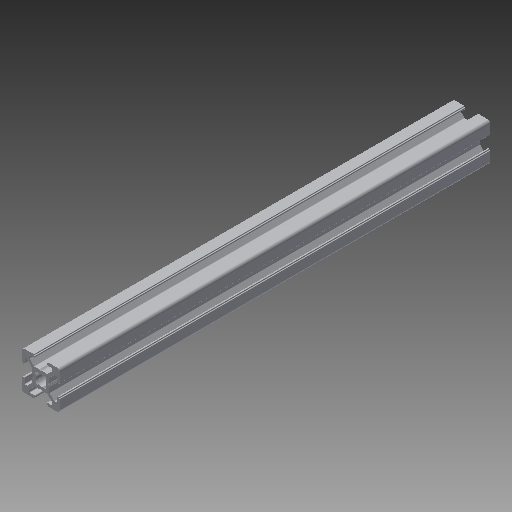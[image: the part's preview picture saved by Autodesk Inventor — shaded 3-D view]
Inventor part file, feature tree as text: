
AUTODESK INVENTOR PART (.ipt)
format: ipt  version: 2017 (Build 210142000, 142)  size: 313,344 bytes
history: native  units: in
note: dims shown in document units (in); Inventor stores cm internally (conversion verified against a paired STEP export)
features: other x3, extrude x1, sketch x1
ambient origin geometry x8: Origin, YZ Plane, XZ Plane, XY Plane, X Axis, Y Axis, Z Axis, Center Point
bodies: Solid1 (feature_tree)
feature tree (5):
  other  "Blocks"
  extrude  "Extrusion1"  [1 undecoded]
  sketch  "Sketch1"  dims[d1=0.0in]
  other  "20x20"
  other  "20x20:1"
note: 1 required parameter value undecoded (feature->parameter linkage not recoverable at this tier; creation-order binding heuristic only, values carry confidence <= 0.55)
